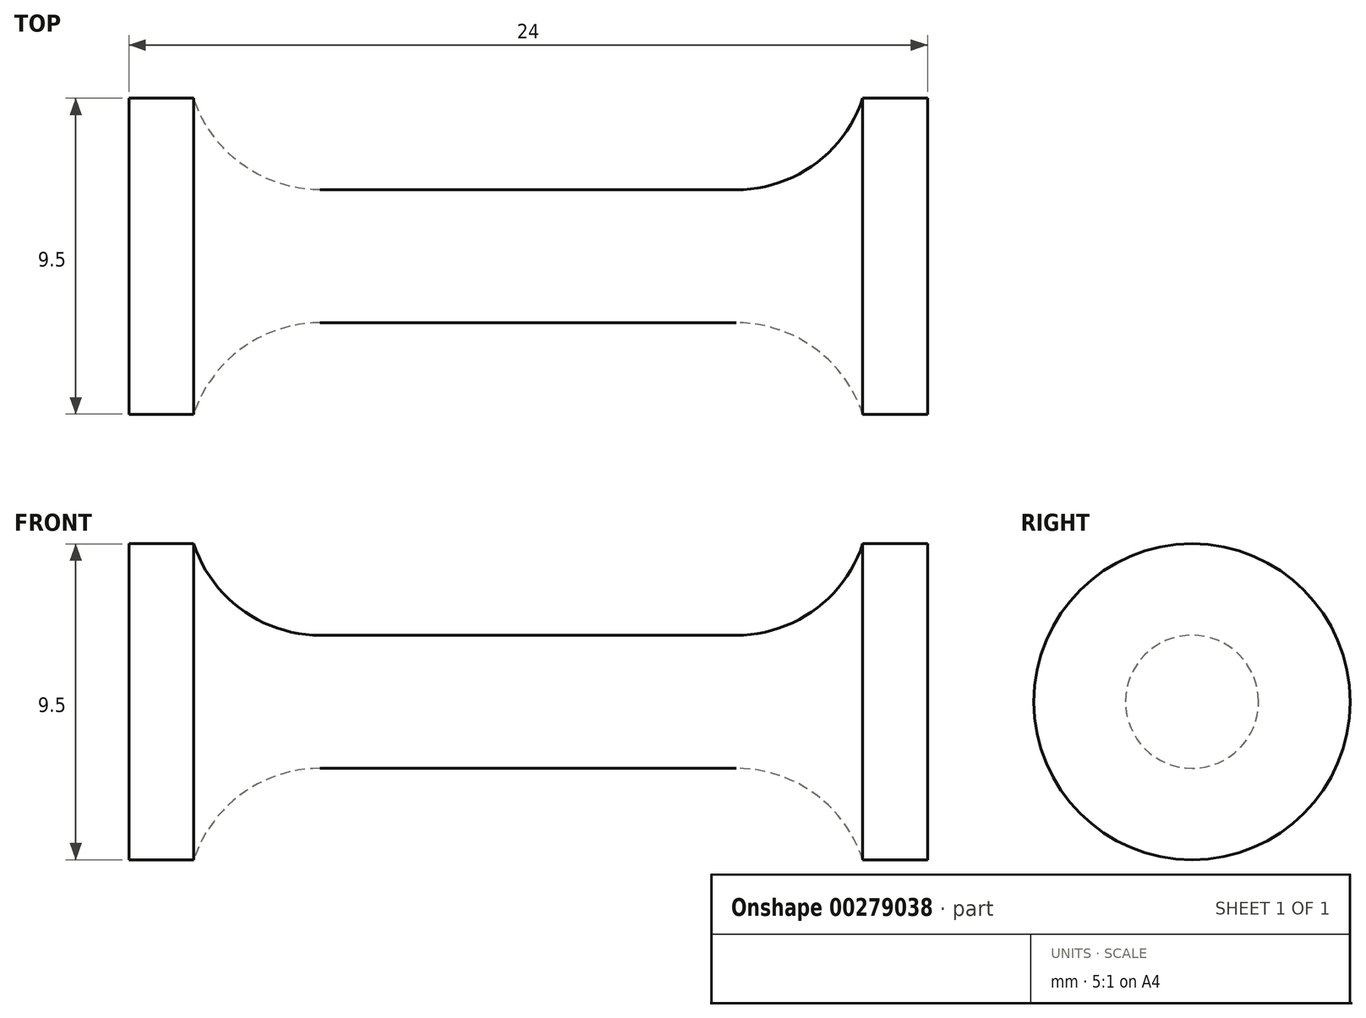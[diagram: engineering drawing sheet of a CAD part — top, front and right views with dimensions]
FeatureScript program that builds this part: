
annotation { "Feature Type Name" : "Feature", "Feature Type Description" : "" }
export const myFeature = defineFeature(function(context is Context, id is Id, definition is map)
    precondition{}
    {
        {
            var Q0;
            Q0=qCreatedBy(makeId("Front.planeOp"),FACE);
            var sketch = newSketch(context, id + "F0", { "sketchPlane" : qUnion([Q0])});
            skLineSegment(sketch, "E0", {"start": v(0, 2) * mm, "end": v(6.25, 2) * mm});
            skArc(sketch, "E1", {"start": v(6.25, 2) * mm, "mid": v(8.6, 2.76) * mm, "end": v(10.05, 4.75) * mm});
            skLineSegment(sketch, "E2", {"start": v(10.05, 4.75) * mm, "end": v(12, 4.75) * mm});
            skLineSegment(sketch, "E3", {"start": v(12, 4.75) * mm, "end": v(12, 0) * mm});
            skLineSegment(sketch, "E4.MirrorCS", {"start": v(0, 2) * mm, "end": v(-6.25, 2) * mm});
            skLineSegment(sketch, "E5.MirrorCS", {"start": v(-12, 4.75) * mm, "end": v(-12, 0) * mm});
            skLineSegment(sketch, "E6.MirrorCS", {"start": v(-10.05, 4.75) * mm, "end": v(-12, 4.75) * mm});
            skArc(sketch, "E7.MirrorCS", {"start": v(-6.25, 2) * mm, "mid": v(-8.6, 2.76) * mm, "end": v(-10.05, 4.75) * mm});
            skLineSegment(sketch, "E8", {"start": v(-12, 0) * mm, "end": v(12, 0) * mm});
            skSolve(sketch);
        }
        {
            var Q0;
            Q0=makeQuery(id+"F0.imprint","IMPRINT",FACE,{"disambiguationData":[TD([[makeQuery(id+"F0.imprint","IMPRINT",EDGE,{"derivedFrom":sQuery(id+"F0.wireOp",EDGE,"E0")}),-1.0]])]});
            var Q1;
            Q1=sQuery(id+"F0.wireOp",EDGE,"E8");
            revolve(context, id + "F1", {"entities" : qUnion([Q0]), "axis" : qUnion([Q1]), "revolveType" : RevolveType.FULL});
        }
    });
